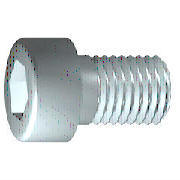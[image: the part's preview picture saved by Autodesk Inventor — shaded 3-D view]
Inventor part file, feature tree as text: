
AUTODESK INVENTOR PART (.ipt)
format: ipt  version: 2020 (Build 240168000, 168)  size: 201,216 bytes
history: native  units: mm (DEFAULTED — no unit token found)
features: sketch x2, extrude x1, plane x1, fillet x1
ambient origin geometry x7: Origin, YZ Plane, XY Plane, X Axis, Y Axis, Z Axis, Center Point
bodies: Solid1 (feature_tree)
feature tree (5):
  extrude  "슬롯"  Depth=6.0mm
  plane  "Work Plane1"
  fillet  "Fillet2"  Radius=0.49086mm
  sketch  "스케치1"
  sketch  "스케치2"
